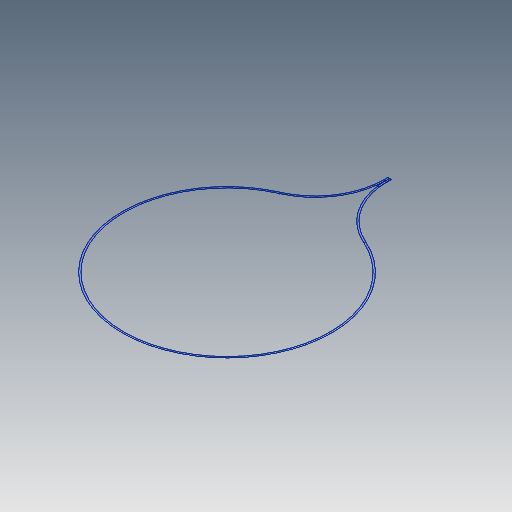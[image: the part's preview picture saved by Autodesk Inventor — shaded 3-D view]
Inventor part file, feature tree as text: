
AUTODESK INVENTOR PART (.ipt)
format: ipt  version: 2020 (Build 240168000, 168)  size: 349,696 bytes
history: native  units: mm
features: sketch x12, extrude x8, projected_geometry x5, fillet x2, sweep x2, chamfer x1, boolean_combine x1, shell x1
ambient origin geometry x8: Origin, YZ Plane, XZ Plane, XY Plane, X Axis, Y Axis, Z Axis, Center Point
bodies: Solid2 (feature_tree), Solid3 (feature_tree)
feature tree (32):
  extrude  "Extrusion12"  Depth=1.3mm
  chamfer  "Chamfer1"  Distance=2.0mm Angle=45.0deg
  sketch  "Sketch13"  dims[d28=140.0mm]
  extrude  "Extrusion13"  Depth=0.15mm
  extrude  "Extrusion14"  Depth=0.15mm
  extrude  "Extrusion15"  TaperAngle=0.0deg  [1 undecoded]
  fillet  "Fillet2"  Radius=6.15mm
  extrude  "Extrusion16"  Depth=0.15mm
  boolean_combine  "Combine1"
  shell  "Shell1"  Thickness=0.0mm
  extrude  "Extrusion17"  Depth=0.15mm
  extrude  "Extrusion18"  Depth=10.0mm
  sweep  "Sweep1"
  sweep  "Sweep2"
  extrude  "Extrusion20"  Depth=0.15mm TaperAngle=0.0deg
  fillet  "Fillet3"  Radius=3.03mm
  sketch  "Sketch11"  dims[d5=1.3mm d19=100.0mm d20=100.0mm d21=1.3mm d22=1.3mm]
  projected_geometry  "Projected Loop11"
  sketch  "Sketch14"  dims[d80=200.0mm]
  sketch  "Sketch15"  dims[d81=45.0deg]
  sketch  "Sketch16"  dims[d82=200.0mm]
  sketch  "Sketch17"  dims[d83=10.0mm]
  projected_geometry  "Projected Loop12"
  sketch  "Sketch19"  dims[d84=0.0mm]
  projected_geometry  "Projected Loop14"
  sketch  "Sketch20"  dims[d85=25.4mm d86=2.0mm d87=45.0deg]
  projected_geometry  "Projected Loop15"
  sketch  "3D Sketch1"
  sketch  "Sketch21"  dims[d97=1.3mm d98=1.3mm d99=1.3mm d100=100.0mm d101=100.0mm d102=150.0mm d103=3.0mm d105=90.0mm d106=3.0mm d107=1.0mm d108=11.0mm d109=145.0mm d110=0.15mm d111=17.960512mm]
  projected_geometry  "Projected Loop16"
  sketch  "3D Sketch2"
  sketch  "Sketch24"  dims[d112=35.921024mm d113=1.15mm d114=0.0mm d115=6.15mm d116=0.0mm d117=9.0mm d118=0.0mm d119=0.65mm d120=10.0mm d121=0.0mm d122=0.15mm d123=194.562mm d124=0.0mm d125=3.03mm d126=0.0mm d127=0.0mm d128=0.0mm d129=0.0mm d130=0.0mm d134=400.0mm d135=400.0mm d136=0.35mm d137=0.0mm d138=0.15mm]
note: 1 required parameter value undecoded (feature->parameter linkage not recoverable at this tier; creation-order binding heuristic only, values carry confidence <= 0.55)
